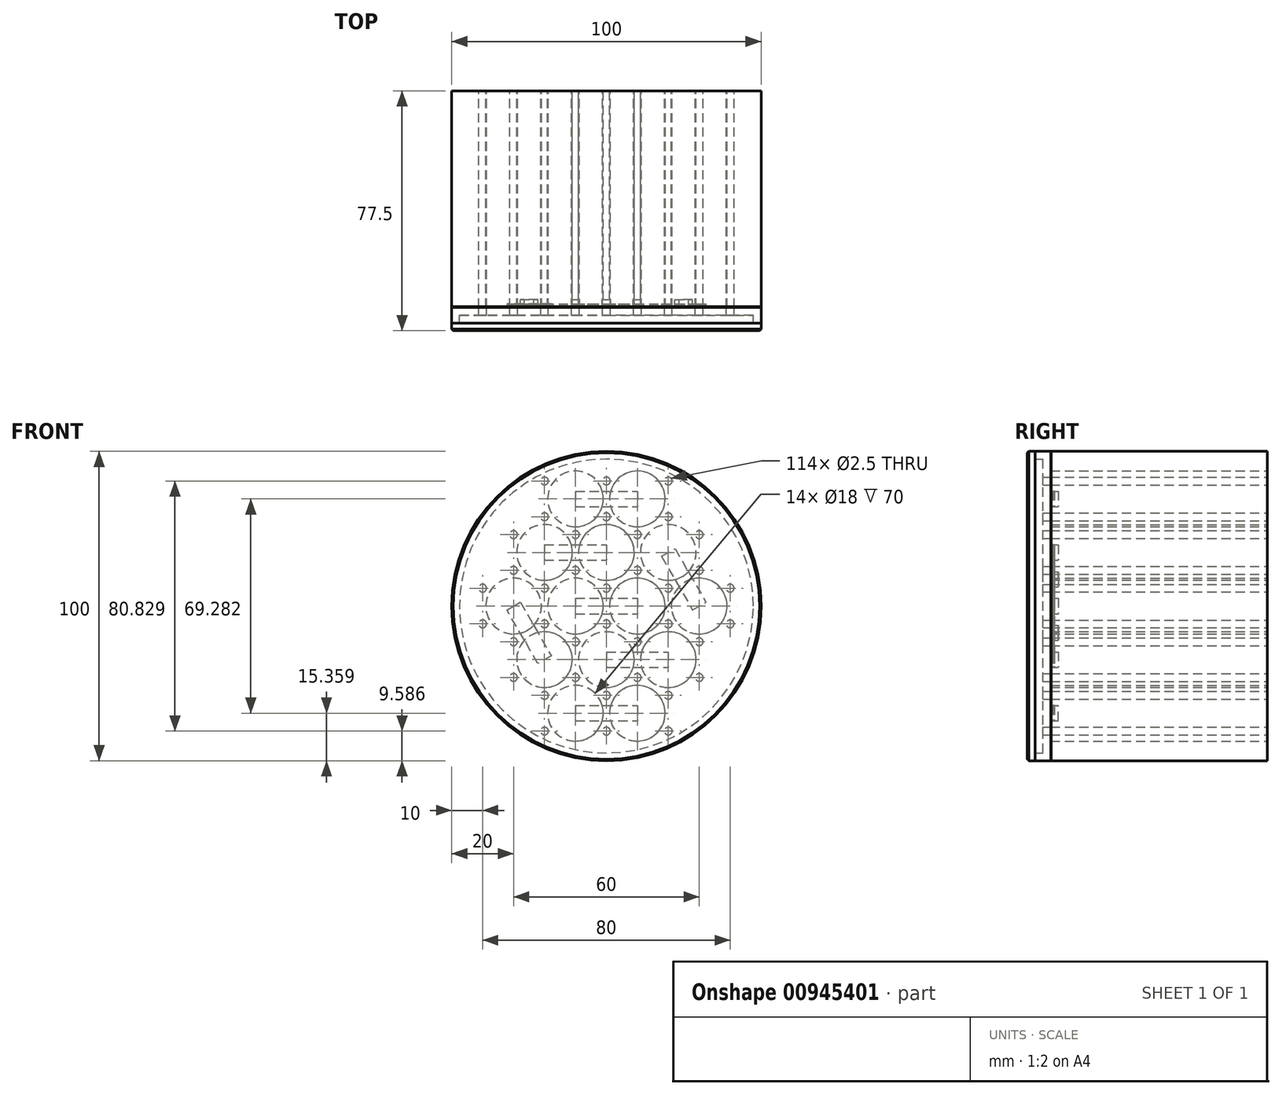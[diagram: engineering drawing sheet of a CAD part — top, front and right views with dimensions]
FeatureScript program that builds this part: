
annotation { "Feature Type Name" : "Feature", "Feature Type Description" : "" }
export const myFeature = defineFeature(function(context is Context, id is Id, definition is map)
    precondition{}
    {
        {
            var Q0;
            Q0=qCreatedBy(makeId("Front.planeOp"),FACE);
            var sketch = newSketch(context, id + "F0", { "sketchPlane" : qUnion([Q0])});
            skCircle(sketch, "E0", {"center": v(0, 0) * mm, "radius": 9 * mm});
            skCircle(sketch, "E1.1.0.0", {"center": v(20, 0) * mm, "radius": 9 * mm});
            skCircle(sketch, "E1.2.0.0", {"center": v(40, 0) * mm, "radius": 9 * mm});
            skCircle(sketch, "E1.3.0.0", {"center": v(60, 0) * mm, "radius": 9 * mm});
            skLineSegment(sketch, "E1.direction1", {"start": v(0, 0) * mm, "end": v(20, 0) * mm, "construction": true});
            skCircle(sketch, "E2", {"center": v(10, 17.32) * mm, "radius": 9 * mm});
            skCircle(sketch, "E3.1.0.0", {"center": v(30, 17.32) * mm, "radius": 9 * mm});
            skCircle(sketch, "E3.2.0.0", {"center": v(50, 17.32) * mm, "radius": 9 * mm});
            skLineSegment(sketch, "E3.direction1", {"start": v(10, 17.32) * mm, "end": v(30, 17.32) * mm, "construction": true});
            skCircle(sketch, "E4", {"center": v(20, 34.64) * mm, "radius": 9 * mm});
            skCircle(sketch, "E5.1.0.0", {"center": v(40, 34.64) * mm, "radius": 9 * mm});
            skLineSegment(sketch, "E5.direction1", {"start": v(20, 34.64) * mm, "end": v(40, 34.64) * mm, "construction": true});
            skCircle(sketch, "E6.MirrorC", {"center": v(10, -17.32) * mm, "radius": 9 * mm});
            skCircle(sketch, "E7.MirrorC", {"center": v(30, -17.32) * mm, "radius": 9 * mm});
            skCircle(sketch, "E8.MirrorC", {"center": v(40, -34.64) * mm, "radius": 9 * mm});
            skCircle(sketch, "E9.MirrorC", {"center": v(20, -34.64) * mm, "radius": 9 * mm});
            skCircle(sketch, "E10.MirrorC", {"center": v(50, -17.32) * mm, "radius": 9 * mm});
            skCircle(sketch, "E11", {"center": v(30, 0) * mm, "radius": 50 * mm});
            skSolve(sketch);
        }
        {
            var Q0;
            Q0=qCreatedBy(makeId("Front.planeOp"),FACE);
            var sketch = newSketch(context, id + "F1", { "sketchPlane" : qUnion([Q0])});
            skCircle(sketch, "E12", {"center": v(-10, 5.77) * mm, "radius": 1.25 * mm});
            skCircle(sketch, "E13.1.0.0", {"center": v(10, 5.77) * mm, "radius": 1.25 * mm});
            skCircle(sketch, "E13.2.0.0", {"center": v(30, 5.77) * mm, "radius": 1.25 * mm});
            skLineSegment(sketch, "E13.direction1", {"start": v(-10, 5.77) * mm, "end": v(10, 5.77) * mm, "construction": true});
            skCircle(sketch, "E14.0.3.0", {"center": v(50, 5.77) * mm, "radius": 1.25 * mm});
            skCircle(sketch, "E14.0.4.0", {"center": v(70, 5.77) * mm, "radius": 1.25 * mm});
            skCircle(sketch, "E15", {"center": v(0, 11.55) * mm, "radius": 1.25 * mm});
            skCircle(sketch, "E16.1.0.0", {"center": v(20, 11.55) * mm, "radius": 1.25 * mm});
            skCircle(sketch, "E16.2.0.0", {"center": v(40, 11.55) * mm, "radius": 1.25 * mm});
            skCircle(sketch, "E16.3.0.0", {"center": v(60, 11.55) * mm, "radius": 1.25 * mm});
            skLineSegment(sketch, "E16.direction1", {"start": v(0, 11.55) * mm, "end": v(20, 11.55) * mm, "construction": true});
            skCircle(sketch, "E17", {"center": v(10, 28.87) * mm, "radius": 1.25 * mm});
            skCircle(sketch, "E18.0", {"center": v(10, 17.32) * mm, "radius": 9 * mm, "construction": true});
            skCircle(sketch, "E19.0", {"center": v(0, 0) * mm, "radius": 9 * mm, "construction": true});
            skCircle(sketch, "E20.0", {"center": v(20, 0) * mm, "radius": 9 * mm, "construction": true});
            skCircle(sketch, "E21.1.0.0", {"center": v(30, 28.87) * mm, "radius": 1.25 * mm});
            skCircle(sketch, "E21.2.0.0", {"center": v(50, 28.87) * mm, "radius": 1.25 * mm});
            skLineSegment(sketch, "E21.direction1", {"start": v(10, 28.87) * mm, "end": v(30, 28.87) * mm, "construction": true});
            skCircle(sketch, "E22", {"center": v(0, 23.1) * mm, "radius": 1.25 * mm});
            skCircle(sketch, "E23.1.0.0", {"center": v(20, 23.1) * mm, "radius": 1.25 * mm});
            skCircle(sketch, "E23.2.0.0", {"center": v(40, 23.1) * mm, "radius": 1.25 * mm});
            skLineSegment(sketch, "E23.direction1", {"start": v(0, 23.1) * mm, "end": v(20, 23.1) * mm, "construction": true});
            skCircle(sketch, "E24.0.3.0", {"center": v(60, 23.1) * mm, "radius": 1.25 * mm});
            skCircle(sketch, "E25", {"center": v(10, 40.41) * mm, "radius": 1.25 * mm});
            skCircle(sketch, "E26.1.0.0", {"center": v(30, 40.41) * mm, "radius": 1.25 * mm});
            skCircle(sketch, "E26.2.0.0", {"center": v(50, 40.41) * mm, "radius": 1.25 * mm});
            skLineSegment(sketch, "E26.direction1", {"start": v(10, 40.41) * mm, "end": v(30, 40.41) * mm, "construction": true});
            skLineSegment(sketch, "E27", {"start": v(0, 0) * mm, "end": v(10, 17.32) * mm, "construction": true});
            skLineSegment(sketch, "E28", {"start": v(5, 8.66) * mm, "end": v(23.02, -1.74) * mm});
            skLineSegment(sketch, "E29", {"start": v(5, 8.66) * mm, "end": v(-5.68, 14.83) * mm});
            skPoint(sketch, "E30.0", {"position": v(20, 34.64) * mm});
            skLineSegment(sketch, "E31", {"start": v(20, 34.64) * mm, "end": v(10, 17.32) * mm, "construction": true});
            skLineSegment(sketch, "E32", {"start": v(15, 25.98) * mm, "end": v(32, 16.16) * mm, "construction": true});
            skLineSegment(sketch, "E33", {"start": v(15, 25.98) * mm, "end": v(2.65, 33.11) * mm, "construction": true});
            skLineSegment(sketch, "E34", {"start": v(20, 34.64) * mm, "end": v(30, 51.96) * mm, "construction": true});
            skLineSegment(sketch, "E35", {"start": v(25, 43.3) * mm, "end": v(37.16, 36.28) * mm, "construction": true});
            skCircle(sketch, "E36.MirrorC", {"center": v(-10, -5.77) * mm, "radius": 1.25 * mm});
            skCircle(sketch, "E37.MirrorC", {"center": v(10, -5.77) * mm, "radius": 1.25 * mm});
            skCircle(sketch, "E38.MirrorC", {"center": v(30, -5.77) * mm, "radius": 1.25 * mm});
            skCircle(sketch, "E39.MirrorC", {"center": v(50, -5.77) * mm, "radius": 1.25 * mm});
            skCircle(sketch, "E40.MirrorC", {"center": v(70, -5.77) * mm, "radius": 1.25 * mm});
            skCircle(sketch, "E41.MirrorC", {"center": v(60, -11.55) * mm, "radius": 1.25 * mm});
            skCircle(sketch, "E42.MirrorC", {"center": v(40, -11.55) * mm, "radius": 1.25 * mm});
            skCircle(sketch, "E43.MirrorC", {"center": v(20, -11.55) * mm, "radius": 1.25 * mm});
            skCircle(sketch, "E44.MirrorC", {"center": v(0, -11.55) * mm, "radius": 1.25 * mm});
            skCircle(sketch, "E45.MirrorC", {"center": v(0, -23.1) * mm, "radius": 1.25 * mm});
            skCircle(sketch, "E46.MirrorC", {"center": v(10, -28.87) * mm, "radius": 1.25 * mm});
            skCircle(sketch, "E47.MirrorC", {"center": v(20, -23.1) * mm, "radius": 1.25 * mm});
            skCircle(sketch, "E48.MirrorC", {"center": v(30, -28.87) * mm, "radius": 1.25 * mm});
            skCircle(sketch, "E49.MirrorC", {"center": v(40, -23.1) * mm, "radius": 1.25 * mm});
            skCircle(sketch, "E50.MirrorC", {"center": v(50, -28.87) * mm, "radius": 1.25 * mm});
            skCircle(sketch, "E51.MirrorC", {"center": v(10, -40.41) * mm, "radius": 1.25 * mm});
            skCircle(sketch, "E52.MirrorC", {"center": v(30, -40.41) * mm, "radius": 1.25 * mm});
            skCircle(sketch, "E53.MirrorC", {"center": v(50, -40.41) * mm, "radius": 1.25 * mm});
            skCircle(sketch, "E54.MirrorC", {"center": v(60, -23.1) * mm, "radius": 1.25 * mm});
            skSolve(sketch);
        }
        {
            var Q0;
            Q0=makeQuery(id+"F0.imprint","IMPRINT",FACE,{"disambiguationData":[TD([[makeQuery(id+"F0.imprint","IMPRINT",EDGE,{"derivedFrom":sQuery(id+"F0.wireOp",EDGE,"E0")}),-1.0]])]});
            extrude(context, id + "F2", {"entities" : qUnion([Q0]), "depth" : 70 * mm, "offsetDistance" : 25 * mm});
        }
        {
            var Q0;
            Q0 = qSketchRegion(id + "F1", true);
            var Q1;
            Q1=makeQuery(id+"F2.opExtrude","CAP_FACE",FACE,{"disambiguationData":[OSD([sQuery(id+"F0.wireOp",EDGE,"E0"),sQuery(id+"F0.wireOp",EDGE,"E1.1.0.0"),sQuery(id+"F0.wireOp",EDGE,"E1.2.0.0"),sQuery(id+"F0.wireOp",EDGE,"E1.3.0.0"),sQuery(id+"F0.wireOp",EDGE,"E2"),sQuery(id+"F0.wireOp",EDGE,"E3.1.0.0"),sQuery(id+"F0.wireOp",EDGE,"E3.2.0.0"),sQuery(id+"F0.wireOp",EDGE,"E4"),sQuery(id+"F0.wireOp",EDGE,"E5.1.0.0"),sQuery(id+"F0.wireOp",EDGE,"E6.MirrorC"),sQuery(id+"F0.wireOp",EDGE,"E7.MirrorC"),sQuery(id+"F0.wireOp",EDGE,"E8.MirrorC"),sQuery(id+"F0.wireOp",EDGE,"E9.MirrorC"),sQuery(id+"F0.wireOp",EDGE,"E10.MirrorC"),sQuery(id+"F0.wireOp",EDGE,"E11")])],"isStart":false});
            extrude(context, id + "F3", {"entities" : qUnion([Q0]), "operationType" : NewBodyOperationType.REMOVE, "endBound" : BoundingType.UP_TO_SURFACE, "depth" : 25 * mm, "endBoundEntityFace" : qUnion([Q1]), "offsetDistance" : 25 * mm});
        }
        {
            var Q0;
            Q0=makeQuery(id+"F2.opExtrude","CAP_FACE",FACE,{"disambiguationData":[OSD([sQuery(id+"F0.wireOp",EDGE,"E0"),sQuery(id+"F0.wireOp",EDGE,"E1.1.0.0"),sQuery(id+"F0.wireOp",EDGE,"E1.2.0.0"),sQuery(id+"F0.wireOp",EDGE,"E1.3.0.0"),sQuery(id+"F0.wireOp",EDGE,"E2"),sQuery(id+"F0.wireOp",EDGE,"E3.1.0.0"),sQuery(id+"F0.wireOp",EDGE,"E3.2.0.0"),sQuery(id+"F0.wireOp",EDGE,"E4"),sQuery(id+"F0.wireOp",EDGE,"E5.1.0.0"),sQuery(id+"F0.wireOp",EDGE,"E6.MirrorC"),sQuery(id+"F0.wireOp",EDGE,"E7.MirrorC"),sQuery(id+"F0.wireOp",EDGE,"E8.MirrorC"),sQuery(id+"F0.wireOp",EDGE,"E9.MirrorC"),sQuery(id+"F0.wireOp",EDGE,"E10.MirrorC"),sQuery(id+"F0.wireOp",EDGE,"E11")])],"isStart":false});
            var sketch = newSketch(context, id + "F4", { "sketchPlane" : qUnion([Q0])});
            skPoint(sketch, "E55.0", {"position": v(20, 34.64) * mm});
            skPoint(sketch, "E56.0", {"position": v(40, 34.64) * mm});
            skPoint(sketch, "E57.0", {"position": v(10, 17.32) * mm});
            skPoint(sketch, "E58.0", {"position": v(30, 17.32) * mm});
            skPoint(sketch, "E59.0", {"position": v(50, 17.32) * mm});
            skPoint(sketch, "E60.0", {"position": v(0, 0) * mm});
            skPoint(sketch, "E61.0", {"position": v(20, 0) * mm});
            skPoint(sketch, "E62.0", {"position": v(40, 0) * mm});
            skLineSegment(sketch, "E63.bottom", {"start": v(20, 37.14) * mm, "end": v(40, 37.14) * mm});
            skLineSegment(sketch, "E63.top", {"start": v(20, 32.14) * mm, "end": v(40, 32.14) * mm});
            skLineSegment(sketch, "E63.left", {"start": v(20, 37.14) * mm, "end": v(20, 32.14) * mm});
            skLineSegment(sketch, "E63.right", {"start": v(40, 37.14) * mm, "end": v(40, 32.14) * mm});
            skLineSegment(sketch, "E64.bottom", {"start": v(10, 19.82) * mm, "end": v(30, 19.82) * mm});
            skLineSegment(sketch, "E64.top", {"start": v(10, 14.82) * mm, "end": v(30, 14.82) * mm});
            skLineSegment(sketch, "E64.left", {"start": v(10, 19.82) * mm, "end": v(10, 14.82) * mm});
            skLineSegment(sketch, "E64.right", {"start": v(30, 19.82) * mm, "end": v(30, 14.82) * mm});
            skLineSegment(sketch, "E65.bottom", {"start": v(20, 2.5) * mm, "end": v(40, 2.5) * mm});
            skLineSegment(sketch, "E65.top", {"start": v(20, -2.5) * mm, "end": v(40, -2.5) * mm});
            skLineSegment(sketch, "E65.left", {"start": v(20, 2.5) * mm, "end": v(20, -2.5) * mm});
            skLineSegment(sketch, "E65.right", {"start": v(40, 2.5) * mm, "end": v(40, -2.5) * mm});
            skPoint(sketch, "E66.0", {"position": v(30, -17.32) * mm});
            skPoint(sketch, "E67.0", {"position": v(50, -17.32) * mm});
            skPoint(sketch, "E68.0", {"position": v(10, -17.32) * mm});
            skPoint(sketch, "E69.0", {"position": v(20, -34.64) * mm});
            skPoint(sketch, "E70.0", {"position": v(40, -34.64) * mm});
            skLineSegment(sketch, "E71.bottom", {"start": v(20, -32.14) * mm, "end": v(40, -32.14) * mm});
            skLineSegment(sketch, "E71.top", {"start": v(20, -37.14) * mm, "end": v(40, -37.14) * mm});
            skLineSegment(sketch, "E71.left", {"start": v(20, -32.14) * mm, "end": v(20, -37.14) * mm});
            skLineSegment(sketch, "E71.right", {"start": v(40, -32.14) * mm, "end": v(40, -37.14) * mm});
            skLineSegment(sketch, "E72.bottom", {"start": v(30, -14.82) * mm, "end": v(50, -14.82) * mm});
            skLineSegment(sketch, "E72.top", {"start": v(30, -19.82) * mm, "end": v(50, -19.82) * mm});
            skLineSegment(sketch, "E72.left", {"start": v(30, -14.82) * mm, "end": v(30, -19.82) * mm});
            skLineSegment(sketch, "E72.right", {"start": v(50, -14.82) * mm, "end": v(50, -19.82) * mm});
            skLineSegment(sketch, "E73", {"start": v(0, 0) * mm, "end": v(10, -17.32) * mm, "construction": true});
            skLineSegment(sketch, "E74", {"start": v(0, 0) * mm, "end": v(2.17, 1.25) * mm});
            skLineSegment(sketch, "E75", {"start": v(2.17, 1.25) * mm, "end": v(12.17, -16.07) * mm});
            skLineSegment(sketch, "E76", {"start": v(12.17, -16.07) * mm, "end": v(7.83, -18.57) * mm});
            skLineSegment(sketch, "E77", {"start": v(7.83, -18.57) * mm, "end": v(-2.18, -1.22) * mm});
            skLineSegment(sketch, "E78", {"start": v(-2.18, -1.22) * mm, "end": v(0, 0) * mm});
            skLineSegment(sketch, "E79", {"start": v(50, 17.32) * mm, "end": v(60, 0) * mm, "construction": true});
            skLineSegment(sketch, "E80", {"start": v(50, 17.32) * mm, "end": v(52.17, 18.57) * mm});
            skLineSegment(sketch, "E81", {"start": v(52.17, 18.57) * mm, "end": v(62.17, 1.25) * mm});
            skLineSegment(sketch, "E82", {"start": v(62.17, 1.25) * mm, "end": v(60, 0) * mm});
            skLineSegment(sketch, "E83", {"start": v(50, 17.32) * mm, "end": v(47.83, 16.07) * mm});
            skLineSegment(sketch, "E84", {"start": v(47.83, 16.07) * mm, "end": v(57.83, -1.25) * mm});
            skLineSegment(sketch, "E85", {"start": v(57.83, -1.25) * mm, "end": v(60, 0) * mm});
            skSolve(sketch);
        }
        {
            var Q0;
            Q0 = qSketchRegion(id + "F4", true);
            extrude(context, id + "F5", {"entities" : qUnion([Q0]), "operationType" : NewBodyOperationType.REMOVE, "oppositeDirection" : true, "depth" : 2.5 * mm, "offsetDistance" : 25 * mm});
        }
        {
            var Q0;
            {var subQ0=sQuery(id+"F4.wireOp",EDGE,"E64.left");Q0=makeQuery(id+"F4.imprint","IMPRINT",FACE,{"disambiguationData":[TD([[makeQuery(id+"F4.imprint","IMPRINT",EDGE,{"derivedFrom":subQ0}),-1.0]])]});}
            var Q1;
            Q1=makeQuery(id+"F4.imprint","IMPRINT",FACE,{"disambiguationData":[TD([[makeQuery(id+"F4.imprint","IMPRINT",EDGE,{"derivedFrom":makeQuery(id+"F2.opExtrude","CAP_EDGE",EDGE,{"disambiguationData":[OSD([sQuery(id+"F0.wireOp",EDGE,"E11")])],"isStart":false})}),1.0]])]});
            var Q2;
            {var subQ0=sQuery(id+"F4.wireOp",EDGE,"E63.left");Q2=makeQuery(id+"F4.imprint","IMPRINT",FACE,{"disambiguationData":[TD([[makeQuery(id+"F4.imprint","IMPRINT",EDGE,{"derivedFrom":subQ0}),-1.0]])]});}
            var Q3;
            {var subQ0=sQuery(id+"F4.wireOp",EDGE,"E64.left");Q3=makeQuery(id+"F4.imprint","IMPRINT",FACE,{"disambiguationData":[TD([[makeQuery(id+"F4.imprint","IMPRINT",EDGE,{"derivedFrom":subQ0}),1.0]])]});}
            var Q4;
            {var subQ0=sQuery(id+"F4.wireOp",EDGE,"E64.bottom");var subQ1=makeQuery(id+"F2.opExtrude","CAP_EDGE",EDGE,{"disambiguationData":[OSD([sQuery(id+"F0.wireOp",EDGE,"E2")])],"isStart":false});var subQ2=makeQuery(id+"F4.imprint","INTERSECT",VERTEX,{"derivedFrom":[subQ1,subQ0]});Q4=makeQuery(id+"F4.imprint","IMPRINT",FACE,{"disambiguationData":[TD([[makeQuery(id+"F4.imprint","IMPRINT",EDGE,{"disambiguationData":[TD([[subQ2,-1.0]])],"derivedFrom":subQ0}),-1.0]])]});}
            var Q5;
            {var subQ0=sQuery(id+"F4.wireOp",EDGE,"E64.right");Q5=makeQuery(id+"F4.imprint","IMPRINT",FACE,{"disambiguationData":[TD([[makeQuery(id+"F4.imprint","IMPRINT",EDGE,{"derivedFrom":subQ0}),-1.0]])]});}
            var Q6;
            {var subQ0=sQuery(id+"F4.wireOp",EDGE,"E64.right");Q6=makeQuery(id+"F4.imprint","IMPRINT",FACE,{"disambiguationData":[TD([[makeQuery(id+"F4.imprint","IMPRINT",EDGE,{"derivedFrom":subQ0}),1.0]])]});}
            var Q7;
            {var subQ0=sQuery(id+"F4.wireOp",EDGE,"E63.bottom");var subQ1=makeQuery(id+"F2.opExtrude","CAP_EDGE",EDGE,{"disambiguationData":[OSD([sQuery(id+"F0.wireOp",EDGE,"E4")])],"isStart":false});var subQ2=makeQuery(id+"F4.imprint","INTERSECT",VERTEX,{"derivedFrom":[subQ1,subQ0]});Q7=makeQuery(id+"F4.imprint","IMPRINT",FACE,{"disambiguationData":[TD([[makeQuery(id+"F4.imprint","IMPRINT",EDGE,{"disambiguationData":[TD([[subQ2,-1.0]])],"derivedFrom":subQ0}),-1.0]])]});}
            var Q8;
            {var subQ0=sQuery(id+"F4.wireOp",EDGE,"E63.left");Q8=makeQuery(id+"F4.imprint","IMPRINT",FACE,{"disambiguationData":[TD([[makeQuery(id+"F4.imprint","IMPRINT",EDGE,{"derivedFrom":subQ0}),1.0]])]});}
            var Q9;
            {var subQ0=sQuery(id+"F4.wireOp",EDGE,"E63.right");Q9=makeQuery(id+"F4.imprint","IMPRINT",FACE,{"disambiguationData":[TD([[makeQuery(id+"F4.imprint","IMPRINT",EDGE,{"derivedFrom":subQ0}),1.0]])]});}
            var Q10;
            {var subQ0=sQuery(id+"F4.wireOp",EDGE,"E63.right");Q10=makeQuery(id+"F4.imprint","IMPRINT",FACE,{"disambiguationData":[TD([[makeQuery(id+"F4.imprint","IMPRINT",EDGE,{"derivedFrom":subQ0}),-1.0]])]});}
            var Q11;
            {var subQ5=sQuery(id+"F4.wireOp",EDGE,"E80");Q11=makeQuery(id+"F4.imprint","IMPRINT",FACE,{"disambiguationData":[TD([[makeQuery(id+"F4.imprint","IMPRINT",EDGE,{"derivedFrom":subQ5}),1.0]])]});}
            var Q12;
            {var subQ6=sQuery(id+"F4.wireOp",EDGE,"E80");Q12=makeQuery(id+"F4.imprint","IMPRINT",FACE,{"disambiguationData":[TD([[makeQuery(id+"F4.imprint","IMPRINT",EDGE,{"derivedFrom":subQ6}),-1.0]])]});}
            var Q13;
            {var subQ0=sQuery(id+"F4.wireOp",EDGE,"E81");var subQ1=makeQuery(id+"F2.opExtrude","CAP_EDGE",EDGE,{"disambiguationData":[OSD([sQuery(id+"F0.wireOp",EDGE,"E3.2.0.0")])],"isStart":false});var subQ2=makeQuery(id+"F4.imprint","INTERSECT",VERTEX,{"derivedFrom":[subQ1,subQ0]});Q13=makeQuery(id+"F4.imprint","IMPRINT",FACE,{"disambiguationData":[TD([[makeQuery(id+"F4.imprint","IMPRINT",EDGE,{"disambiguationData":[TD([[subQ2,-1.0]])],"derivedFrom":subQ0}),-1.0]])]});}
            var Q14;
            {var subQ1=sQuery(id+"F4.wireOp",EDGE,"E82");Q14=makeQuery(id+"F4.imprint","IMPRINT",FACE,{"disambiguationData":[TD([[makeQuery(id+"F4.imprint","IMPRINT",EDGE,{"derivedFrom":subQ1}),-1.0]])]});}
            var Q15;
            {var subQ1=sQuery(id+"F4.wireOp",EDGE,"E82");Q15=makeQuery(id+"F4.imprint","IMPRINT",FACE,{"disambiguationData":[TD([[makeQuery(id+"F4.imprint","IMPRINT",EDGE,{"derivedFrom":subQ1}),1.0]])]});}
            var Q16;
            {var subQ0=sQuery(id+"F4.wireOp",EDGE,"E65.right");Q16=makeQuery(id+"F4.imprint","IMPRINT",FACE,{"disambiguationData":[TD([[makeQuery(id+"F4.imprint","IMPRINT",EDGE,{"derivedFrom":subQ0}),1.0]])]});}
            var Q17;
            {var subQ0=sQuery(id+"F4.wireOp",EDGE,"E65.right");Q17=makeQuery(id+"F4.imprint","IMPRINT",FACE,{"disambiguationData":[TD([[makeQuery(id+"F4.imprint","IMPRINT",EDGE,{"derivedFrom":subQ0}),-1.0]])]});}
            var Q18;
            {var subQ0=sQuery(id+"F4.wireOp",EDGE,"E65.bottom");var subQ1=makeQuery(id+"F2.opExtrude","CAP_EDGE",EDGE,{"disambiguationData":[OSD([sQuery(id+"F0.wireOp",EDGE,"E1.1.0.0")])],"isStart":false});var subQ2=makeQuery(id+"F4.imprint","INTERSECT",VERTEX,{"derivedFrom":[subQ1,subQ0]});Q18=makeQuery(id+"F4.imprint","IMPRINT",FACE,{"disambiguationData":[TD([[makeQuery(id+"F4.imprint","IMPRINT",EDGE,{"disambiguationData":[TD([[subQ2,-1.0]])],"derivedFrom":subQ0}),-1.0]])]});}
            var Q19;
            {var subQ0=sQuery(id+"F4.wireOp",EDGE,"E65.left");Q19=makeQuery(id+"F4.imprint","IMPRINT",FACE,{"disambiguationData":[TD([[makeQuery(id+"F4.imprint","IMPRINT",EDGE,{"derivedFrom":subQ0}),1.0]])]});}
            var Q20;
            {var subQ0=sQuery(id+"F4.wireOp",EDGE,"E65.left");Q20=makeQuery(id+"F4.imprint","IMPRINT",FACE,{"disambiguationData":[TD([[makeQuery(id+"F4.imprint","IMPRINT",EDGE,{"derivedFrom":subQ0}),-1.0]])]});}
            var Q21;
            {var subQ5=sQuery(id+"F4.wireOp",EDGE,"E74");Q21=makeQuery(id+"F4.imprint","IMPRINT",FACE,{"disambiguationData":[TD([[makeQuery(id+"F4.imprint","IMPRINT",EDGE,{"derivedFrom":subQ5}),1.0]])]});}
            var Q22;
            {var subQ5=sQuery(id+"F4.wireOp",EDGE,"E74");Q22=makeQuery(id+"F4.imprint","IMPRINT",FACE,{"disambiguationData":[TD([[makeQuery(id+"F4.imprint","IMPRINT",EDGE,{"derivedFrom":subQ5}),-1.0]])]});}
            var Q23;
            {var subQ0=sQuery(id+"F4.wireOp",EDGE,"E75");var subQ1=makeQuery(id+"F2.opExtrude","CAP_EDGE",EDGE,{"disambiguationData":[OSD([sQuery(id+"F0.wireOp",EDGE,"E0")])],"isStart":false});var subQ2=makeQuery(id+"F4.imprint","INTERSECT",VERTEX,{"derivedFrom":[subQ1,subQ0]});Q23=makeQuery(id+"F4.imprint","IMPRINT",FACE,{"disambiguationData":[TD([[makeQuery(id+"F4.imprint","IMPRINT",EDGE,{"disambiguationData":[TD([[subQ2,-1.0]])],"derivedFrom":subQ0}),-1.0]])]});}
            var Q24;
            {var subQ0=sQuery(id+"F4.wireOp",EDGE,"E76");Q24=makeQuery(id+"F4.imprint","IMPRINT",FACE,{"disambiguationData":[TD([[makeQuery(id+"F4.imprint","IMPRINT",EDGE,{"derivedFrom":subQ0}),-1.0]])]});}
            var Q25;
            {var subQ0=sQuery(id+"F4.wireOp",EDGE,"E76");Q25=makeQuery(id+"F4.imprint","IMPRINT",FACE,{"disambiguationData":[TD([[makeQuery(id+"F4.imprint","IMPRINT",EDGE,{"derivedFrom":subQ0}),1.0]])]});}
            var Q26;
            {var subQ0=sQuery(id+"F4.wireOp",EDGE,"E72.left");Q26=makeQuery(id+"F4.imprint","IMPRINT",FACE,{"disambiguationData":[TD([[makeQuery(id+"F4.imprint","IMPRINT",EDGE,{"derivedFrom":subQ0}),-1.0]])]});}
            var Q27;
            {var subQ0=sQuery(id+"F4.wireOp",EDGE,"E72.left");Q27=makeQuery(id+"F4.imprint","IMPRINT",FACE,{"disambiguationData":[TD([[makeQuery(id+"F4.imprint","IMPRINT",EDGE,{"derivedFrom":subQ0}),1.0]])]});}
            var Q28;
            {var subQ0=sQuery(id+"F4.wireOp",EDGE,"E72.bottom");var subQ1=makeQuery(id+"F2.opExtrude","CAP_EDGE",EDGE,{"disambiguationData":[OSD([sQuery(id+"F0.wireOp",EDGE,"E7.MirrorC")])],"isStart":false});var subQ2=makeQuery(id+"F4.imprint","INTERSECT",VERTEX,{"derivedFrom":[subQ1,subQ0]});Q28=makeQuery(id+"F4.imprint","IMPRINT",FACE,{"disambiguationData":[TD([[makeQuery(id+"F4.imprint","IMPRINT",EDGE,{"disambiguationData":[TD([[subQ2,-1.0]])],"derivedFrom":subQ0}),-1.0]])]});}
            var Q29;
            {var subQ0=sQuery(id+"F4.wireOp",EDGE,"E72.right");Q29=makeQuery(id+"F4.imprint","IMPRINT",FACE,{"disambiguationData":[TD([[makeQuery(id+"F4.imprint","IMPRINT",EDGE,{"derivedFrom":subQ0}),-1.0]])]});}
            var Q30;
            {var subQ0=sQuery(id+"F4.wireOp",EDGE,"E72.right");Q30=makeQuery(id+"F4.imprint","IMPRINT",FACE,{"disambiguationData":[TD([[makeQuery(id+"F4.imprint","IMPRINT",EDGE,{"derivedFrom":subQ0}),1.0]])]});}
            var Q31;
            {var subQ0=sQuery(id+"F4.wireOp",EDGE,"E71.right");Q31=makeQuery(id+"F4.imprint","IMPRINT",FACE,{"disambiguationData":[TD([[makeQuery(id+"F4.imprint","IMPRINT",EDGE,{"derivedFrom":subQ0}),1.0]])]});}
            var Q32;
            {var subQ0=sQuery(id+"F4.wireOp",EDGE,"E71.right");Q32=makeQuery(id+"F4.imprint","IMPRINT",FACE,{"disambiguationData":[TD([[makeQuery(id+"F4.imprint","IMPRINT",EDGE,{"derivedFrom":subQ0}),-1.0]])]});}
            var Q33;
            {var subQ0=sQuery(id+"F4.wireOp",EDGE,"E71.bottom");var subQ1=makeQuery(id+"F2.opExtrude","CAP_EDGE",EDGE,{"disambiguationData":[OSD([sQuery(id+"F0.wireOp",EDGE,"E9.MirrorC")])],"isStart":false});var subQ2=makeQuery(id+"F4.imprint","INTERSECT",VERTEX,{"derivedFrom":[subQ1,subQ0]});Q33=makeQuery(id+"F4.imprint","IMPRINT",FACE,{"disambiguationData":[TD([[makeQuery(id+"F4.imprint","IMPRINT",EDGE,{"disambiguationData":[TD([[subQ2,-1.0]])],"derivedFrom":subQ0}),-1.0]])]});}
            var Q34;
            {var subQ0=sQuery(id+"F4.wireOp",EDGE,"E71.left");Q34=makeQuery(id+"F4.imprint","IMPRINT",FACE,{"disambiguationData":[TD([[makeQuery(id+"F4.imprint","IMPRINT",EDGE,{"derivedFrom":subQ0}),1.0]])]});}
            var Q35;
            {var subQ0=sQuery(id+"F4.wireOp",EDGE,"E71.left");Q35=makeQuery(id+"F4.imprint","IMPRINT",FACE,{"disambiguationData":[TD([[makeQuery(id+"F4.imprint","IMPRINT",EDGE,{"derivedFrom":subQ0}),-1.0]])]});}
            extrude(context, id + "F6", {"entities" : qUnion([Q0, Q1, Q2, Q3, Q4, Q5, Q6, Q7, Q8, Q9, Q10, Q11, Q12, Q13, Q14, Q15, Q16, Q17, Q18, Q19, Q20, Q21, Q22, Q23, Q24, Q25, Q26, Q27, Q28, Q29, Q30, Q31, Q32, Q33, Q34, Q35]), "depth" : 2.5 * mm, "offsetDistance" : 25 * mm});
        }
        {
            var Q0;
            Q0=makeQuery(id+"F6.opExtrude","CAP_FACE",FACE,{"disambiguationData":[OSD([sQuery(id+"F0.wireOp",EDGE,"E0"),sQuery(id+"F0.wireOp",EDGE,"E1.1.0.0"),sQuery(id+"F0.wireOp",EDGE,"E1.2.0.0"),sQuery(id+"F0.wireOp",EDGE,"E1.3.0.0"),sQuery(id+"F0.wireOp",EDGE,"E2"),sQuery(id+"F0.wireOp",EDGE,"E3.1.0.0"),sQuery(id+"F0.wireOp",EDGE,"E3.2.0.0"),sQuery(id+"F0.wireOp",EDGE,"E4"),sQuery(id+"F0.wireOp",EDGE,"E5.1.0.0"),sQuery(id+"F0.wireOp",EDGE,"E6.MirrorC"),sQuery(id+"F0.wireOp",EDGE,"E7.MirrorC"),sQuery(id+"F0.wireOp",EDGE,"E8.MirrorC"),sQuery(id+"F0.wireOp",EDGE,"E9.MirrorC"),sQuery(id+"F0.wireOp",EDGE,"E10.MirrorC"),sQuery(id+"F0.wireOp",EDGE,"E11"),sQuery(id+"F1.wireOp",EDGE,"E12"),sQuery(id+"F1.wireOp",EDGE,"E13.1.0.0"),sQuery(id+"F1.wireOp",EDGE,"E13.2.0.0"),sQuery(id+"F1.wireOp",EDGE,"E14.0.3.0"),sQuery(id+"F1.wireOp",EDGE,"E14.0.4.0"),sQuery(id+"F1.wireOp",EDGE,"E15"),sQuery(id+"F1.wireOp",EDGE,"E16.1.0.0"),sQuery(id+"F1.wireOp",EDGE,"E16.2.0.0"),sQuery(id+"F1.wireOp",EDGE,"E16.3.0.0"),sQuery(id+"F1.wireOp",EDGE,"E17"),sQuery(id+"F1.wireOp",EDGE,"E21.1.0.0"),sQuery(id+"F1.wireOp",EDGE,"E21.2.0.0"),sQuery(id+"F1.wireOp",EDGE,"E22"),sQuery(id+"F1.wireOp",EDGE,"E23.1.0.0"),sQuery(id+"F1.wireOp",EDGE,"E23.2.0.0"),sQuery(id+"F1.wireOp",EDGE,"E24.0.3.0"),sQuery(id+"F1.wireOp",EDGE,"E25"),sQuery(id+"F1.wireOp",EDGE,"E26.1.0.0"),sQuery(id+"F1.wireOp",EDGE,"E26.2.0.0"),sQuery(id+"F1.wireOp",EDGE,"E36.MirrorC"),sQuery(id+"F1.wireOp",EDGE,"E37.MirrorC"),sQuery(id+"F1.wireOp",EDGE,"E38.MirrorC"),sQuery(id+"F1.wireOp",EDGE,"E39.MirrorC"),sQuery(id+"F1.wireOp",EDGE,"E40.MirrorC"),sQuery(id+"F1.wireOp",EDGE,"E41.MirrorC"),sQuery(id+"F1.wireOp",EDGE,"E42.MirrorC"),sQuery(id+"F1.wireOp",EDGE,"E43.MirrorC"),sQuery(id+"F1.wireOp",EDGE,"E44.MirrorC"),sQuery(id+"F1.wireOp",EDGE,"E45.MirrorC"),sQuery(id+"F1.wireOp",EDGE,"E46.MirrorC"),sQuery(id+"F1.wireOp",EDGE,"E47.MirrorC"),sQuery(id+"F1.wireOp",EDGE,"E48.MirrorC"),sQuery(id+"F1.wireOp",EDGE,"E49.MirrorC"),sQuery(id+"F1.wireOp",EDGE,"E50.MirrorC"),sQuery(id+"F1.wireOp",EDGE,"E51.MirrorC"),sQuery(id+"F1.wireOp",EDGE,"E52.MirrorC"),sQuery(id+"F1.wireOp",EDGE,"E53.MirrorC"),sQuery(id+"F1.wireOp",EDGE,"E54.MirrorC")])],"isStart":false});
            var sketch = newSketch(context, id + "F7", { "sketchPlane" : qUnion([Q0])});
            skCircle(sketch, "E86.0", {"center": v(30, 0) * mm, "radius": 50 * mm});
            skCircle(sketch, "E87.0", {"center": v(30, 0) * mm, "radius": 47.5 * mm});
            skSolve(sketch);
        }
        {
            var Q0;
            Q0=makeQuery(id+"F7.imprint","IMPRINT",FACE,{"disambiguationData":[TD([[makeQuery(id+"F7.imprint","IMPRINT",EDGE,{"derivedFrom":sQuery(id+"F7.wireOp",EDGE,"E86.0")}),1.0]])]});
            extrude(context, id + "F8", {"entities" : qUnion([Q0]), "operationType" : NewBodyOperationType.ADD, "depth" : 2.5 * mm, "offsetDistance" : 25 * mm});
        }
        {
            var Q0;
            Q0=makeQuery(id+"F8.opExtrude","CAP_FACE",FACE,{"disambiguationData":[OSD([sQuery(id+"F7.wireOp",EDGE,"E86.0"),sQuery(id+"F7.wireOp",EDGE,"E87.0")])],"isStart":false});
            var sketch = newSketch(context, id + "F9", { "sketchPlane" : qUnion([Q0])});
            skCircle(sketch, "E88.0", {"center": v(30, 0) * mm, "radius": 50 * mm});
            skSolve(sketch);
        }
        {
            var Q0;
            Q0 = qSketchRegion(id + "F9", true);
            extrude(context, id + "F10", {"entities" : qUnion([Q0]), "depth" : 2.5 * mm, "offsetDistance" : 25 * mm});
        }
        {
            var Q0;
            Q0=makeQuery(id+"F10.opExtrude","CAP_EDGE",EDGE,{"disambiguationData":[OSD([sQuery(id+"F9.wireOp",EDGE,"E88.0")])],"isStart":false});
            chamfer(context, id + "F11", {"entities" : qUnion([Q0]), "width" : .5 * mm, "tangentPropagation" : true});
        }
        {
            var Q0;
            Q0=makeQuery(id+"F6.opExtrude","CAP_FACE",FACE,{"disambiguationData":[OSD([sQuery(id+"F0.wireOp",EDGE,"E11"),sQuery(id+"F1.wireOp",EDGE,"E12"),sQuery(id+"F1.wireOp",EDGE,"E13.1.0.0"),sQuery(id+"F1.wireOp",EDGE,"E13.2.0.0"),sQuery(id+"F1.wireOp",EDGE,"E14.0.3.0"),sQuery(id+"F1.wireOp",EDGE,"E14.0.4.0"),sQuery(id+"F1.wireOp",EDGE,"E15"),sQuery(id+"F1.wireOp",EDGE,"E16.1.0.0"),sQuery(id+"F1.wireOp",EDGE,"E16.2.0.0"),sQuery(id+"F1.wireOp",EDGE,"E16.3.0.0"),sQuery(id+"F1.wireOp",EDGE,"E17"),sQuery(id+"F1.wireOp",EDGE,"E21.1.0.0"),sQuery(id+"F1.wireOp",EDGE,"E21.2.0.0"),sQuery(id+"F1.wireOp",EDGE,"E22"),sQuery(id+"F1.wireOp",EDGE,"E23.1.0.0"),sQuery(id+"F1.wireOp",EDGE,"E23.2.0.0"),sQuery(id+"F1.wireOp",EDGE,"E24.0.3.0"),sQuery(id+"F1.wireOp",EDGE,"E25"),sQuery(id+"F1.wireOp",EDGE,"E26.1.0.0"),sQuery(id+"F1.wireOp",EDGE,"E26.2.0.0"),sQuery(id+"F1.wireOp",EDGE,"E36.MirrorC"),sQuery(id+"F1.wireOp",EDGE,"E37.MirrorC"),sQuery(id+"F1.wireOp",EDGE,"E38.MirrorC"),sQuery(id+"F1.wireOp",EDGE,"E39.MirrorC"),sQuery(id+"F1.wireOp",EDGE,"E40.MirrorC"),sQuery(id+"F1.wireOp",EDGE,"E41.MirrorC"),sQuery(id+"F1.wireOp",EDGE,"E42.MirrorC"),sQuery(id+"F1.wireOp",EDGE,"E43.MirrorC"),sQuery(id+"F1.wireOp",EDGE,"E44.MirrorC"),sQuery(id+"F1.wireOp",EDGE,"E45.MirrorC"),sQuery(id+"F1.wireOp",EDGE,"E46.MirrorC"),sQuery(id+"F1.wireOp",EDGE,"E47.MirrorC"),sQuery(id+"F1.wireOp",EDGE,"E48.MirrorC"),sQuery(id+"F1.wireOp",EDGE,"E49.MirrorC"),sQuery(id+"F1.wireOp",EDGE,"E50.MirrorC"),sQuery(id+"F1.wireOp",EDGE,"E51.MirrorC"),sQuery(id+"F1.wireOp",EDGE,"E52.MirrorC"),sQuery(id+"F1.wireOp",EDGE,"E53.MirrorC"),sQuery(id+"F1.wireOp",EDGE,"E54.MirrorC")])],"isStart":true});
            extrude(context, id + "F12", {"entities" : qUnion([Q0]), "depth" : .25 * mm, "offsetDistance" : 25 * mm});
        }
        {
            var Q0;
            Q0 = qSketchRegion(id + "F4", true);
            extrude(context, id + "F13", {"entities" : qUnion([Q0]), "oppositeDirection" : true, "depth" : 1.2 * mm, "offsetDistance" : 25 * mm, "hasSecondDirection" : true, "secondDirectionOppositeDirection" : true, "secondDirectionDepth" : 0.83 * mm});
        }
    });
